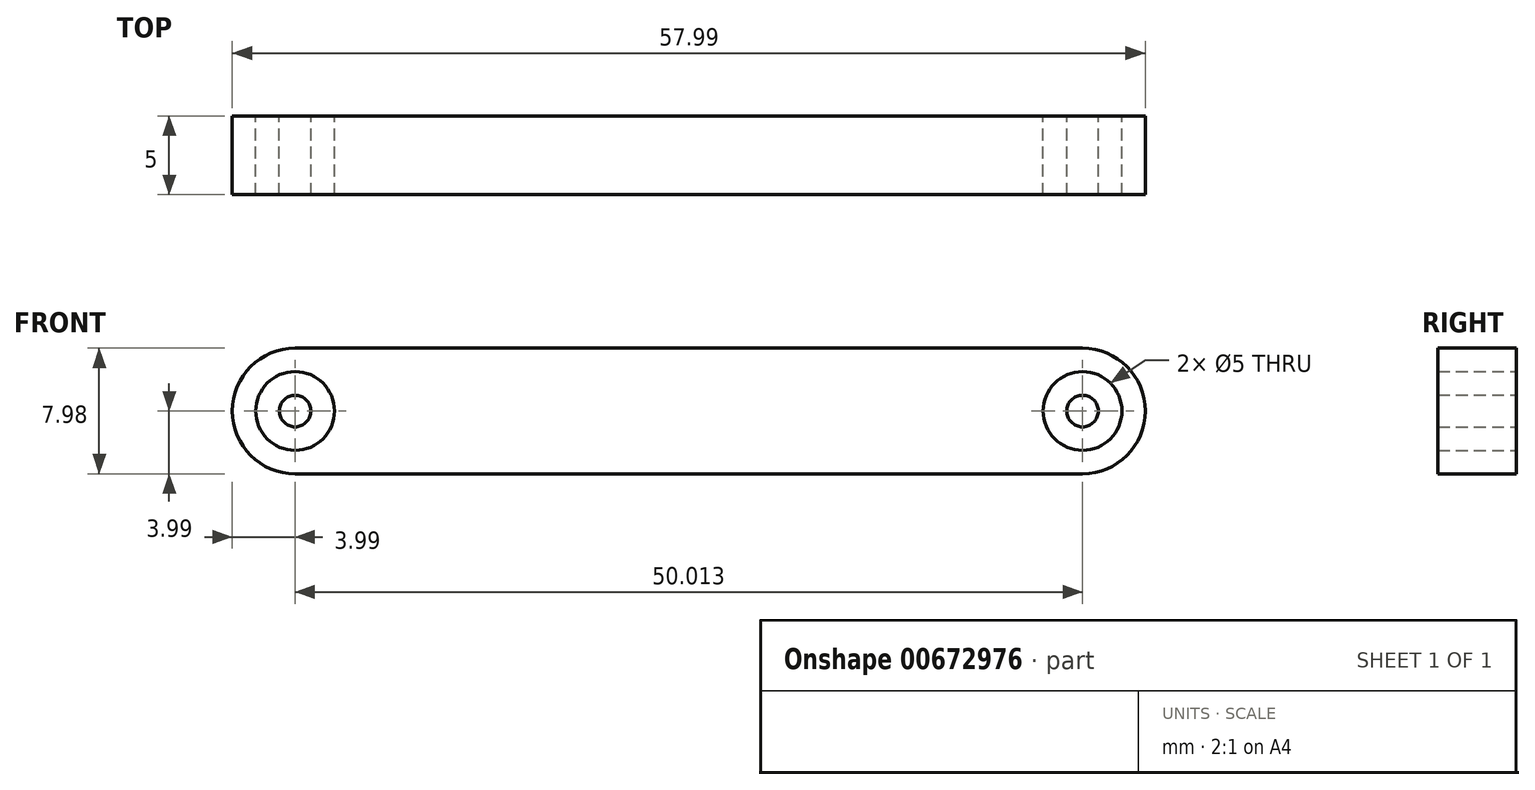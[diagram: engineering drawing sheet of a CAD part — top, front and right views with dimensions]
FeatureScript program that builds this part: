
annotation { "Feature Type Name" : "Feature", "Feature Type Description" : "" }
export const myFeature = defineFeature(function(context is Context, id is Id, definition is map)
    precondition{}
    {
        {
            var Q0;
            Q0=qCreatedBy(makeId("Front.planeOp"),FACE);
            var sketch = newSketch(context, id + "F0", { "sketchPlane" : qUnion([Q0])});
            skArc(sketch, "E0", {"start": v(0, 3.99) * mm, "mid": v(-3.99, 0) * mm, "end": v(0, -3.99) * mm});
            skArc(sketch, "E1", {"start": v(50.01, -3.99) * mm, "mid": v(54, 0) * mm, "end": v(50.01, 3.99) * mm});
            skCircle(sketch, "E2", {"center": v(50.01, 0) * mm, "radius": 2.5 * mm});
            skCircle(sketch, "E3", {"center": v(50.01, 0) * mm, "radius": 1 * mm});
            skCircle(sketch, "E4", {"center": v(0, 0) * mm, "radius": 2.5 * mm});
            skCircle(sketch, "E5", {"center": v(0, 0) * mm, "radius": 1 * mm});
            skLineSegment(sketch, "E6", {"start": v(0, 3.99) * mm, "end": v(50.01, 3.99) * mm});
            skLineSegment(sketch, "E7", {"start": v(50.01, -3.99) * mm, "end": v(0, -3.99) * mm});
            skSolve(sketch);
        }
        {
            var Q0;
            Q0 = qSketchRegion(id + "F0", true);
            var Q1;
            Q1=makeQuery(id+"F0.imprint","IMPRINT",FACE,{"disambiguationData":[TD([[makeQuery(id+"F0.imprint","IMPRINT",EDGE,{"derivedFrom":sQuery(id+"F0.wireOp",EDGE,"E5")}),1.0]])]});
            var Q2;
            Q2=makeQuery(id+"F0.imprint","IMPRINT",FACE,{"disambiguationData":[TD([[makeQuery(id+"F0.imprint","IMPRINT",EDGE,{"derivedFrom":sQuery(id+"F0.wireOp",EDGE,"E3")}),1.0]])]});
            extrude(context, id + "F1", {"entities" : qUnion([Q0, Q1, Q2]), "depth" : 5 * mm, "offsetDistance" : 25.4 * mm});
        }
    });
